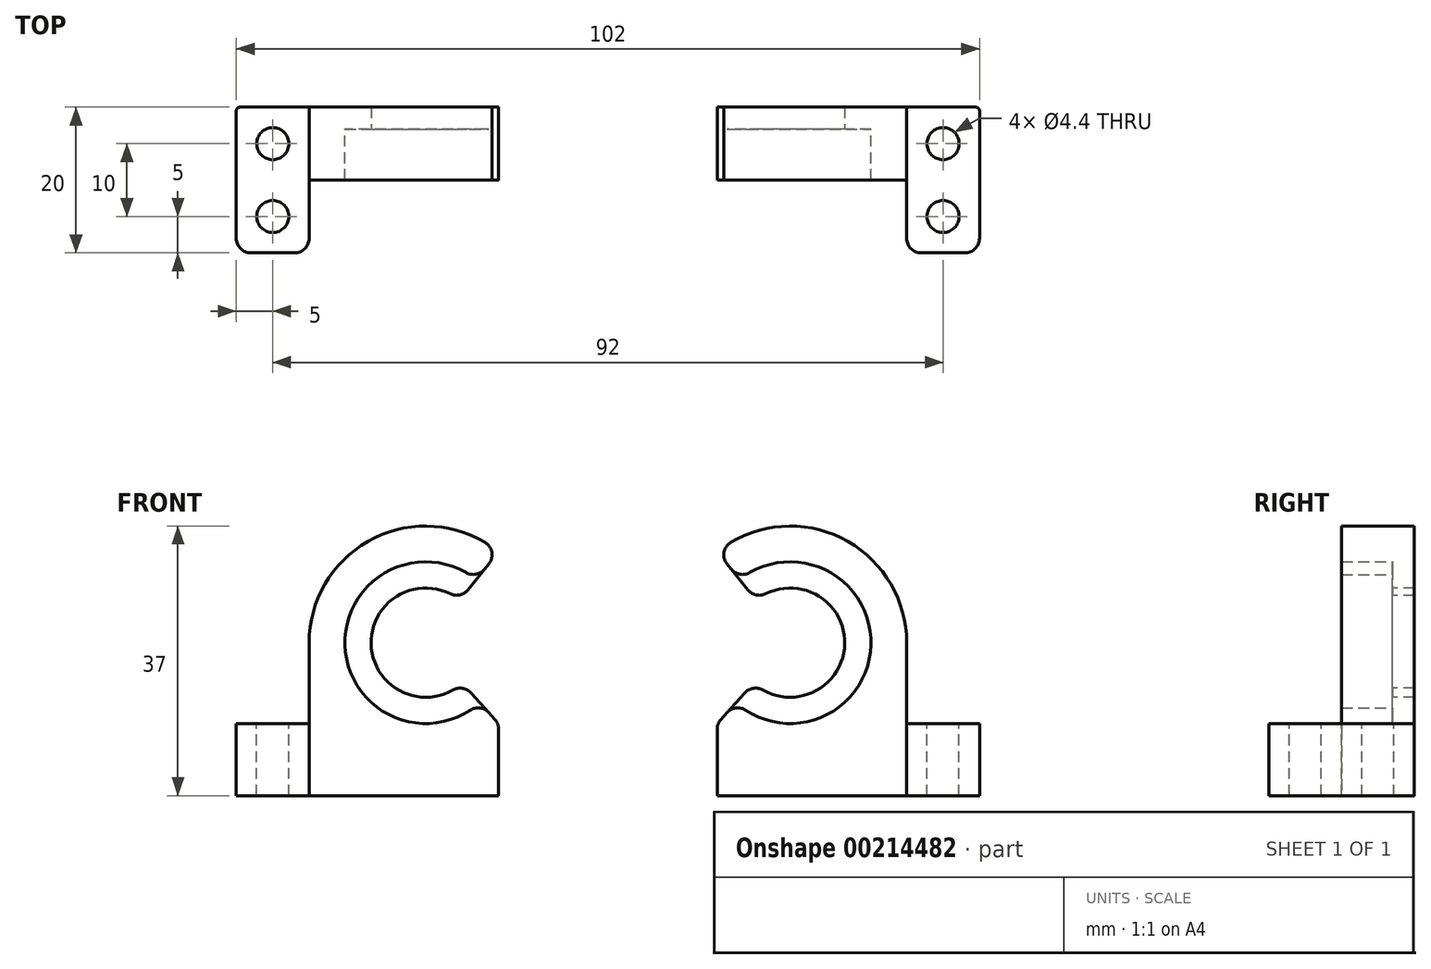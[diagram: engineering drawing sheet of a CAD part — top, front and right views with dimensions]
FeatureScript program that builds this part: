
annotation { "Feature Type Name" : "Feature", "Feature Type Description" : "" }
export const myFeature = defineFeature(function(context is Context, id is Id, definition is map)
    precondition{}
    {
        {
            var Q0;
            Q0=qCreatedBy(makeId("Front.planeOp"),FACE);
            var sketch = newSketch(context, id + "F0", { "sketchPlane" : qUnion([Q0])});
            skLineSegment(sketch, "E0.bottom", {"start": v(-26, 16) * mm, "end": v(26, 16) * mm});
            skLineSegment(sketch, "E0.top", {"start": v(-26, -21) * mm, "end": v(26, -21) * mm});
            skLineSegment(sketch, "E0.left", {"start": v(-26, 16) * mm, "end": v(-26, -21) * mm});
            skLineSegment(sketch, "E0.right", {"start": v(26, 16) * mm, "end": v(26, -21) * mm});
            skPoint(sketch, "E0.middle", {"position": v(0, -2.5) * mm});
            skCircle(sketch, "E1", {"center": v(0, 0) * mm, "radius": 11.1 * mm});
            skCircle(sketch, "E2", {"center": v(0, 0) * mm, "radius": 16 * mm});
            skLineSegment(sketch, "E3", {"start": v(-26, -11.1) * mm, "end": v(26, -11.1) * mm});
            skLineSegment(sketch, "E4", {"start": v(16, 0) * mm, "end": v(16, -11.1) * mm});
            skCircle(sketch, "E5", {"center": v(0, 0) * mm, "radius": 7.5 * mm});
            skLineSegment(sketch, "E6", {"start": v(-10, 16) * mm, "end": v(-10, -21) * mm, "construction": true});
            skLineSegment(sketch, "E7", {"start": v(-10, 12.49) * mm, "end": v(0, 0) * mm, "construction": true});
            skLineSegment(sketch, "E8", {"start": v(-10, 12.49) * mm, "end": v(-4.69, 5.85) * mm});
            skLineSegment(sketch, "E9", {"start": v(0, 0) * mm, "end": v(-10, -11.1) * mm, "construction": true});
            skLineSegment(sketch, "E10", {"start": v(-10, -11.1) * mm, "end": v(-5.02, -5.57) * mm});
            skLineSegment(sketch, "E11", {"start": v(-10, -11.1) * mm, "end": v(-10, -21) * mm});
            skSolve(sketch);
        }
        {
            var Q0;
            {var subQ8=sQuery(id+"F0.wireOp",EDGE,"E11");Q0=makeQuery(id+"F0.imprint","IMPRINT",FACE,{"disambiguationData":[TD([[makeQuery(id+"F0.imprint","IMPRINT",EDGE,{"derivedFrom":subQ8}),1.0]])]});}
            var Q1;
            {var subQ0=sQuery(id+"F0.wireOp",EDGE,"E4");Q1=makeQuery(id+"F0.imprint","IMPRINT",FACE,{"disambiguationData":[TD([[makeQuery(id+"F0.imprint","IMPRINT",EDGE,{"derivedFrom":subQ0}),-1.0]])]});}
            var Q2;
            {var subQ4=sQuery(id+"F0.wireOp",EDGE,"E8");var subQ7=sQuery(id+"F0.wireOp",EDGE,"E1");var subQ8=makeQuery(id+"F0.imprint","INTERSECT",VERTEX,{"derivedFrom":[subQ7,subQ4]});Q2=makeQuery(id+"F0.imprint","IMPRINT",FACE,{"disambiguationData":[TD([[makeQuery(id+"F0.imprint","IMPRINT",EDGE,{"disambiguationData":[TD([[subQ8,1.0]])],"derivedFrom":subQ7}),-1.0]])]});}
            var Q3;
            {var subQ0=sQuery(id+"F0.wireOp",EDGE,"E10");var subQ1=sQuery(id+"F0.wireOp",EDGE,"E1");var subQ2=makeQuery(id+"F0.imprint","INTERSECT",VERTEX,{"derivedFrom":[subQ1,subQ0]});Q3=makeQuery(id+"F0.imprint","IMPRINT",FACE,{"disambiguationData":[TD([[makeQuery(id+"F0.imprint","IMPRINT",EDGE,{"disambiguationData":[TD([[subQ2,-1.0]])],"derivedFrom":subQ1}),-1.0]])]});}
            var Q4;
            {var subQ6=sQuery(id+"F0.wireOp",EDGE,"E0.right");var subQ7=sQuery(id+"F0.wireOp",EDGE,"E0.top");var subQ8=makeQuery(id+"F0.imprint","INTERSECT",VERTEX,{"derivedFrom":[subQ7,subQ6]});Q4=makeQuery(id+"F0.imprint","IMPRINT",FACE,{"disambiguationData":[TD([[makeQuery(id+"F0.imprint","IMPRINT",EDGE,{"disambiguationData":[TD([[subQ8,1.0]])],"derivedFrom":subQ7}),1.0]])]});}
            var Q5;
            {var subQ0=sQuery(id+"F0.wireOp",EDGE,"opkqvmq9-LnvV-yUsD-LyPu-0UFfAWLlyz0K");Q5=makeQuery(id+"F0.imprint","IMPRINT",FACE,{"disambiguationData":[TD([[makeQuery(id+"F0.imprint","IMPRINT",EDGE,{"derivedFrom":subQ0}),-1.0]])]});}
            extrude(context, id + "F1", {"entities" : qUnion([Q0, Q1, Q2, Q3, Q4, Q5]), "depth" : 7 * mm});
        }
        {
            var Q0;
            Q0=makeQuery(id+"F1.opExtrude","CAP_FACE",FACE,{"disambiguationData":[OSD([sQuery(id+"F0.wireOp",EDGE,"E0.top"),sQuery(id+"F0.wireOp",EDGE,"E0.right"),sQuery(id+"F0.wireOp",EDGE,"E1"),sQuery(id+"F0.wireOp",EDGE,"E2"),sQuery(id+"F0.wireOp",EDGE,"E3"),sQuery(id+"F0.wireOp",EDGE,"E4"),sQuery(id+"F0.wireOp",EDGE,"E8"),sQuery(id+"F0.wireOp",EDGE,"E10"),sQuery(id+"F0.wireOp",EDGE,"E11")])],"isStart":true});
            var Q1;
            {var subQ3=sQuery(id+"F0.wireOp",EDGE,"E1");var subQ5=sQuery(id+"F0.wireOp",EDGE,"E10");var subQ8=makeQuery(id+"F0.imprint","INTERSECT",VERTEX,{"derivedFrom":[subQ3,subQ5]});Q1=makeQuery(id+"F0.imprint","IMPRINT",FACE,{"disambiguationData":[TD([[makeQuery(id+"F0.imprint","IMPRINT",EDGE,{"disambiguationData":[TD([[subQ8,-1.0]])],"derivedFrom":subQ3}),1.0]])]});}
            extrude(context, id + "F2", {"entities" : qUnion([Q0, Q1]), "operationType" : NewBodyOperationType.ADD, "depth" : 3 * mm});
        }
        {
            var Q0;
            Q0=makeQuery(id+"F1.opExtrude","CAP_FACE",FACE,{"disambiguationData":[OSD([sQuery(id+"F0.wireOp",EDGE,"E0.top"),sQuery(id+"F0.wireOp",EDGE,"E0.right"),sQuery(id+"F0.wireOp",EDGE,"E1"),sQuery(id+"F0.wireOp",EDGE,"E2"),sQuery(id+"F0.wireOp",EDGE,"E3"),sQuery(id+"F0.wireOp",EDGE,"E4"),sQuery(id+"F0.wireOp",EDGE,"E8"),sQuery(id+"F0.wireOp",EDGE,"E10"),sQuery(id+"F0.wireOp",EDGE,"E11")])],"isStart":false});
            var sketch = newSketch(context, id + "F3", { "sketchPlane" : qUnion([Q0])});
            skLineSegment(sketch, "E12.bottom", {"start": v(26, -21) * mm, "end": v(16, -21) * mm});
            skLineSegment(sketch, "E12.top", {"start": v(26, -11.1) * mm, "end": v(16, -11.1) * mm});
            skLineSegment(sketch, "E12.left", {"start": v(26, -21) * mm, "end": v(26, -11.1) * mm});
            skLineSegment(sketch, "E12.right", {"start": v(16, -21) * mm, "end": v(16, -11.1) * mm});
            skSolve(sketch);
        }
        {
            var Q0;
            Q0 = qSketchRegion(id + "F3", true);
            extrude(context, id + "F4", {"entities" : qUnion([Q0]), "operationType" : NewBodyOperationType.ADD, "depth" : 10 * mm});
        }
        {
            var Q0;
            {var subQ0=sQuery(id+"F0.wireOp",EDGE,"E3");Q0=makeQuery(id+"F4.boolean.opBoolean","MERGE",FACE,{"derivedFrom":[makeQuery(id+"F2.boolean.opBoolean","MERGE",FACE,{"derivedFrom":[makeQuery(id+"F1.opExtrude","SWEPT_FACE",FACE,{"disambiguationData":[OSD([subQ0])]}),makeQuery(id+"F2.opExtrude","SWEPT_FACE",FACE,{"disambiguationData":[OSD([subQ0])]})]}),makeQuery(id+"F4.opExtrude","SWEPT_FACE",FACE,{"disambiguationData":[OSD([sQuery(id+"F3.wireOp",EDGE,"E12.top")])]})]});}
            var sketch = newSketch(context, id + "F5", { "sketchPlane" : qUnion([Q0])});
            skLineSegment(sketch, "E13", {"start": v(26, -7) * mm, "end": v(16, -7) * mm, "construction": true});
            skPoint(sketch, "E14", {"position": v(21, -2) * mm});
            skPoint(sketch, "E14.positionSnap0", {"position": v(21, -7) * mm});
            skPoint(sketch, "E15.MirrorP", {"position": v(21, -12) * mm});
            skSolve(sketch);
        }
        {
            var Q0;
            Q0=sQuery(id+"F5.wireOp",VERTEX,"E14");
            var Q1;
            Q1=sQuery(id+"F5.wireOp",VERTEX,"E15.MirrorP");
            var Q2;
            Q2=makeQuery(id+"F1.opExtrude","SWEPT_BODY",BODY,{"disambiguationData":[OSD([sQuery(id+"F0.wireOp",EDGE,"E0.top"),sQuery(id+"F0.wireOp",EDGE,"E0.right"),sQuery(id+"F0.wireOp",EDGE,"E1"),sQuery(id+"F0.wireOp",EDGE,"E2"),sQuery(id+"F0.wireOp",EDGE,"E3"),sQuery(id+"F0.wireOp",EDGE,"E4"),sQuery(id+"F0.wireOp",EDGE,"E8"),sQuery(id+"F0.wireOp",EDGE,"E10"),sQuery(id+"F0.wireOp",EDGE,"E11")])]});
            hole(context, id + "F6", {"style" : HoleStyle.SIMPLE, "endStyle" : HoleEndStyle.THROUGH, "standardTappedOrClearance" : lookupTablePath({ "standard" : "ISO", "fit" : "Normal", "size" : "M4", "type" : "Clearance" }), "standardBlindInLast" : lookupTablePath({ "fit" : "Standard", "standard" : "ISO", "size" : "M4", "type" : "Clearance" }), "holeDiameter" : 4.4 * mm, "locations" : qUnion([Q0, Q1]), "scope" : qUnion([Q2]), "isTappedThrough" : true});
        }
        {
            var Q0;
            {var subQ0=sQuery(id+"F0.wireOp",EDGE,"E8");var subQ1=sQuery(id+"F0.wireOp",EDGE,"E2");Q0=makeQuery(id+"F2.boolean.opBoolean","MERGE",EDGE,{"derivedFrom":[makeQuery(id+"F1.opExtrude","SWEPT_EDGE",EDGE,{"disambiguationData":[OSD([subQ1,subQ0])]}),makeQuery(id+"F2.opExtrude","SWEPT_EDGE",EDGE,{"disambiguationData":[OSD([subQ1,subQ0])]})]});}
            var Q1;
            Q1=makeQuery(id+"F2.opExtrude","SWEPT_EDGE",EDGE,{"disambiguationData":[OSD([sQuery(id+"F0.wireOp",EDGE,"E5"),sQuery(id+"F0.wireOp",EDGE,"E8")])]});
            var Q2;
            Q2=makeQuery(id+"F2.opExtrude","SWEPT_EDGE",EDGE,{"disambiguationData":[OSD([sQuery(id+"F0.wireOp",EDGE,"E5"),sQuery(id+"F0.wireOp",EDGE,"E10")])]});
            var Q3;
            Q3=makeQuery(id+"F1.opExtrude","SWEPT_EDGE",EDGE,{"disambiguationData":[OSD([sQuery(id+"F0.wireOp",EDGE,"E1"),sQuery(id+"F0.wireOp",EDGE,"E10")])]});
            var Q4;
            Q4=makeQuery(id+"F1.opExtrude","SWEPT_EDGE",EDGE,{"disambiguationData":[OSD([sQuery(id+"F0.wireOp",EDGE,"E1"),sQuery(id+"F0.wireOp",EDGE,"E8")])]});
            var Q5;
            {var subQ0=sQuery(id+"F0.wireOp",EDGE,"E11");var subQ1=sQuery(id+"F0.wireOp",EDGE,"E10");var subQ2=sQuery(id+"F0.wireOp",EDGE,"E3");Q5=makeQuery(id+"F2.boolean.opBoolean","MERGE",EDGE,{"derivedFrom":[makeQuery(id+"F1.opExtrude","SWEPT_EDGE",EDGE,{"disambiguationData":[OSD([subQ2,subQ1,subQ0])]}),makeQuery(id+"F2.opExtrude","SWEPT_EDGE",EDGE,{"disambiguationData":[OSD([subQ2,subQ1,subQ0])]})]});}
            fillet(context, id + "F7", {"entities" : qUnion([Q0, Q1, Q2, Q3, Q4, Q5]), "radius" : 2 * mm, "tangentPropagation" : true, "allowEdgeOverflow" : false});
        }
        {
            var Q0;
            Q0=makeQuery(id+"F4.opExtrude","CAP_EDGE",EDGE,{"disambiguationData":[OSD([sQuery(id+"F3.wireOp",EDGE,"E12.right")])],"isStart":false});
            var Q1;
            Q1=makeQuery(id+"F4.opExtrude","CAP_EDGE",EDGE,{"disambiguationData":[OSD([sQuery(id+"F3.wireOp",EDGE,"E12.right")])],"isStart":true});
            var Q2;
            Q2=makeQuery(id+"F4.opExtrude","CAP_EDGE",EDGE,{"disambiguationData":[OSD([sQuery(id+"F3.wireOp",EDGE,"E12.left")])],"isStart":false});
            fillet(context, id + "F8", {"entities" : qUnion([Q0, Q1, Q2]), "radius" : 2 * mm, "tangentPropagation" : true, "allowEdgeOverflow" : false});
        }
        {
            var Q0;
            Q0=makeQuery(id+"F2.opExtrude","CAP_EDGE",EDGE,{"disambiguationData":[OSD([sQuery(id+"F0.wireOp",EDGE,"E0.right")])],"isStart":false});
            fillet(context, id + "F9", {"entities" : qUnion([Q0]), "radius" : 0.5 * mm, "tangentPropagation" : true, "allowEdgeOverflow" : false});
        }
        {
            var Q0;
            Q0=qCreatedBy(makeId("Right.planeOp"),FACE);
            cPlane(context, id + "F10", {"entities" : qUnion([Q0]), "cplaneType" : CPlaneType.OFFSET, "offset" : 25 * mm, "oppositeDirection" : true, "width" : 150 * mm, "height" : 150 * mm});
        }
        {
            var Q0;
            Q0=makeQuery(id+"F1.opExtrude","SWEPT_BODY",BODY,{"disambiguationData":[OSD([sQuery(id+"F0.wireOp",EDGE,"E0.top"),sQuery(id+"F0.wireOp",EDGE,"E0.right"),sQuery(id+"F0.wireOp",EDGE,"E1"),sQuery(id+"F0.wireOp",EDGE,"E2"),sQuery(id+"F0.wireOp",EDGE,"E3"),sQuery(id+"F0.wireOp",EDGE,"E4"),sQuery(id+"F0.wireOp",EDGE,"E8"),sQuery(id+"F0.wireOp",EDGE,"E10"),sQuery(id+"F0.wireOp",EDGE,"E11")])]});
            var Q1;
            Q1=qCreatedBy(id+"F10.planeOp",FACE);
            mirror(context, id + "F11", {"entities" : qUnion([Q0]), "mirrorPlane" : qUnion([Q1])});
        }
    });
